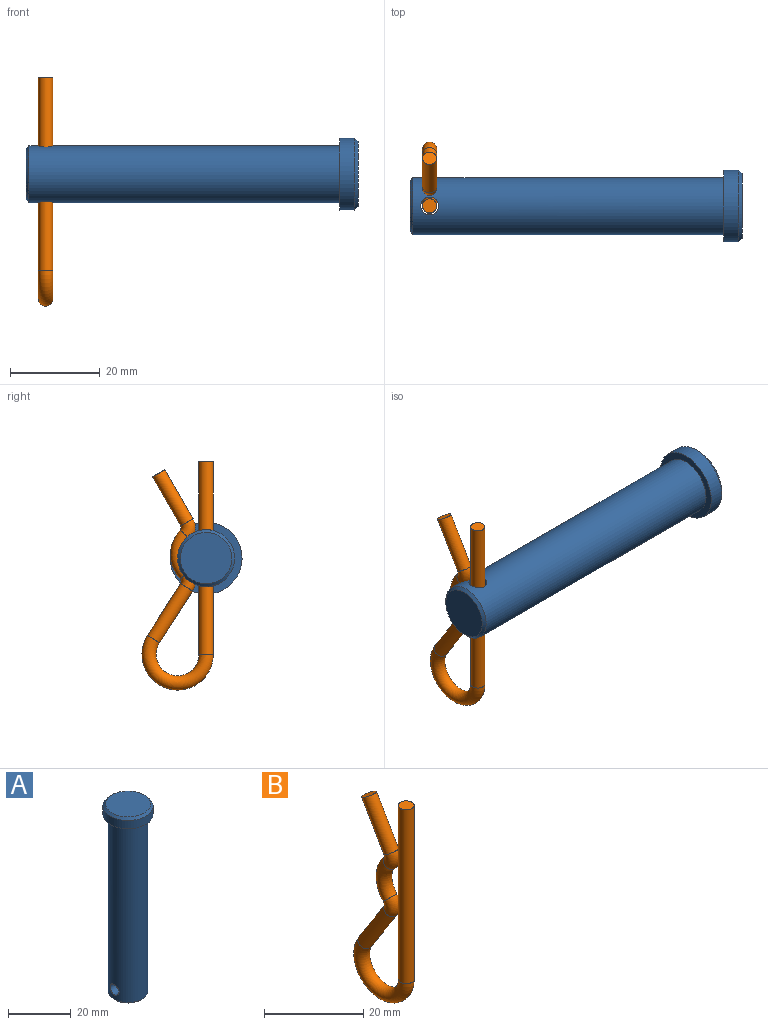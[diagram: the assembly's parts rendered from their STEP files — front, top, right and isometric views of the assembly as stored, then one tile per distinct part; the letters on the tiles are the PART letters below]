
ASSEMBLY  parts=2 mates=1
PART A: 8 faces, bbox 16x16x73.9 mm
  f0: cone r=6.35mm half-angle=45deg, axis (0,0,1), area 34mm2, adj f4,f5
  f1: cylinder r=1.98mm len=12.7mm, axis (1,0,0), area 154.4mm2, adj f4
  f2: cone r=7.19mm half-angle=45deg, axis (0,0,-1), area 54.9mm2, adj f3,f7
  f3: cylinder r=8mm len=16mm, axis (0,0,-1), area 163.4mm2, adj f2,f6
  f4: cylinder r=6.35mm len=69.22mm, axis (0,0,-1), area 2736.5mm2, adj f0,f1,f6
  f5: plane 11.43x11.43mm, normal (0,0,-1), area 102.6mm2, adj f0
  f6: plane 16x16mm, normal (0,0,-1), area 74.4mm2, adj f3,f4
  f7: plane 14.38x14.38mm, normal (0,0,1), area 162.3mm2, adj f2
PART B: 9 faces, bbox 3.2x17.2x51.5 mm
  f0: torus R=6.35mm, axis (1,0,0), area 235mm2, adj f4,f5
  f1: torus R=2.38mm, axis (-1,0,0), area 31.5mm2, adj f2,f5
  f2: torus R=6.35mm, axis (1,0,0), area 95.8mm2, adj f1,f3
  f3: torus R=2.38mm, axis (-1,0,0), area 30.4mm2, adj f2,f6
  f4: cylinder r=1.59mm len=42.86mm, axis (0,0,1), area 427.5mm2, adj f0,f8
  f5: cylinder r=1.59mm len=13.24mm, axis (0,-0.54,0.84), area 136.5mm2, adj f0,f1
  f6: cylinder r=1.59mm len=12.5mm, axis (0,0.5,0.87), area 125.7mm2, adj f3,f7
  f7: plane 3.18x2.75mm, normal (0,0.5,0.87), area 7.9mm2, adj f6
  f8: plane 3.18x3.18mm, normal (0,0,1), area 7.9mm2, adj f4
PLACE A rot(axis=(0.71,0,0.71),180deg) t=(14.68,0,-21.43)mm
PLACE B at identity
MATE fastened A.f1 <-> B.f4  axis (0,0,1) through (0,0,-21.43)mm
